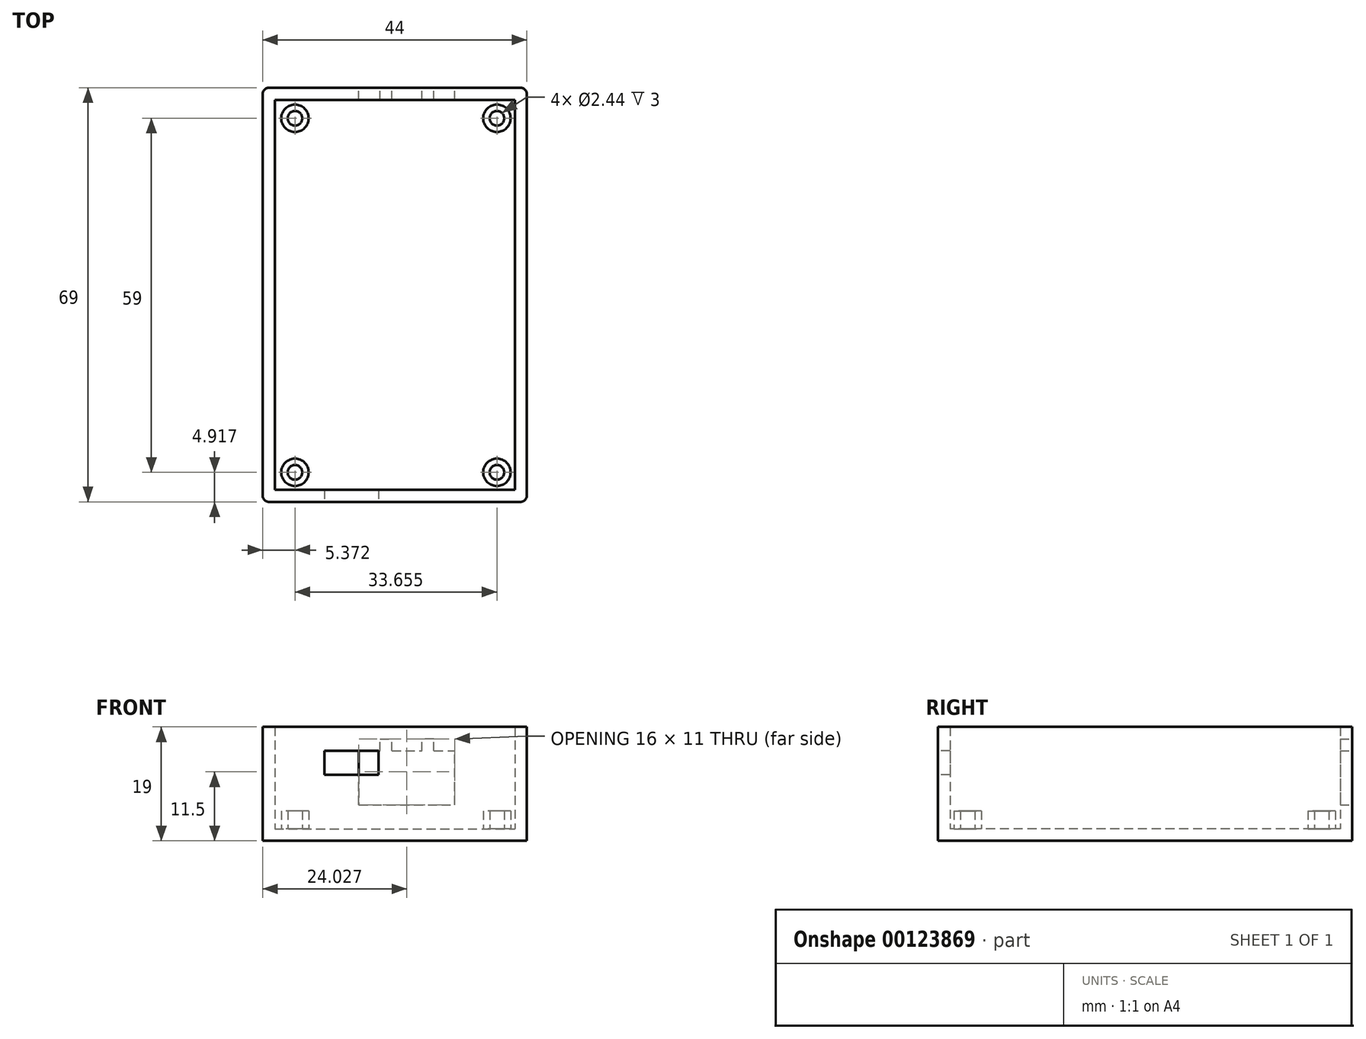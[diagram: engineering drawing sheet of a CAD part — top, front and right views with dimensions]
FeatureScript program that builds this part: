
annotation { "Feature Type Name" : "Feature", "Feature Type Description" : "" }
export const myFeature = defineFeature(function(context is Context, id is Id, definition is map)
    precondition{}
    {
        {
            var Q0;
            Q0=qCreatedBy(makeId("Top.planeOp"),FACE);
            var sketch = newSketch(context, id + "F0", { "sketchPlane" : qUnion([Q0])});
            skLineSegment(sketch, "E0.bottom", {"start": v(20, -32.5) * mm, "end": v(-20, -32.5) * mm});
            skLineSegment(sketch, "E0.top", {"start": v(20, 32.5) * mm, "end": v(-20, 32.5) * mm});
            skLineSegment(sketch, "E0.left", {"start": v(20, -32.5) * mm, "end": v(20, 32.5) * mm});
            skLineSegment(sketch, "E0.right", {"start": v(-20, -32.5) * mm, "end": v(-20, 32.5) * mm});
            skPoint(sketch, "E0.middle", {"position": v(0, 0) * mm});
            skLineSegment(sketch, "E1.0", {"start": v(21, 34.5) * mm, "end": v(-21, 34.5) * mm});
            skLineSegment(sketch, "E1.1", {"start": v(22, -33.5) * mm, "end": v(22, 33.5) * mm});
            skLineSegment(sketch, "E1.2", {"start": v(21, -34.5) * mm, "end": v(-21, -34.5) * mm});
            skLineSegment(sketch, "E1.3", {"start": v(-22, -33.5) * mm, "end": v(-22, 33.5) * mm});
            skCircle(sketch, "E2", {"center": v(-16.63, 29.42) * mm, "radius": 2.28 * mm});
            skCircle(sketch, "E3", {"center": v(-16.63, 29.42) * mm, "radius": 1.22 * mm});
            skCircle(sketch, "E4.0.1.0", {"center": v(-16.63, -29.58) * mm, "radius": 2.28 * mm});
            skCircle(sketch, "E4.0.1.1", {"center": v(-16.63, -29.58) * mm, "radius": 1.22 * mm});
            skCircle(sketch, "E4.1.0.0", {"center": v(17.03, 29.42) * mm, "radius": 2.28 * mm});
            skCircle(sketch, "E4.1.0.1", {"center": v(17.03, 29.42) * mm, "radius": 1.22 * mm});
            skCircle(sketch, "E4.1.1.0", {"center": v(17.03, -29.58) * mm, "radius": 2.28 * mm});
            skCircle(sketch, "E4.1.1.1", {"center": v(17.03, -29.58) * mm, "radius": 1.22 * mm});
            skLineSegment(sketch, "E4.direction1", {"start": v(-16.63, 29.42) * mm, "end": v(17.03, 29.42) * mm, "construction": true});
            skLineSegment(sketch, "E4.direction2", {"start": v(-16.63, 29.42) * mm, "end": v(-16.63, -29.58) * mm, "construction": true});
            skPoint(sketch, "E5.visualSharp", {"position": v(-22, 34.5) * mm});
            skArc(sketch, "E5.filletArc", {"start": v(-21, 34.5) * mm, "mid": v(-21.7, 34.2) * mm, "end": v(-22, 33.5) * mm});
            skPoint(sketch, "E6.visualSharp", {"position": v(22, 34.5) * mm});
            skArc(sketch, "E6.filletArc", {"start": v(22, 33.5) * mm, "mid": v(21.7, 34.2) * mm, "end": v(21, 34.5) * mm});
            skPoint(sketch, "E7.visualSharp", {"position": v(-22, -34.5) * mm});
            skArc(sketch, "E7.filletArc", {"start": v(-22, -33.5) * mm, "mid": v(-21.7, -34.2) * mm, "end": v(-21, -34.5) * mm});
            skPoint(sketch, "E8.visualSharp", {"position": v(22, -34.5) * mm});
            skArc(sketch, "E8.filletArc", {"start": v(21, -34.5) * mm, "mid": v(21.7, -34.2) * mm, "end": v(22, -33.5) * mm});
            skSolve(sketch);
        }
        {
            var Q0;
            Q0=makeQuery(id+"F0.imprint","IMPRINT",FACE,{"disambiguationData":[TD([[makeQuery(id+"F0.imprint","IMPRINT",EDGE,{"derivedFrom":sQuery(id+"F0.wireOp",EDGE,"E0.bottom")}),1.0]])]});
            var Q1;
            Q1=makeQuery(id+"F0.imprint","IMPRINT",FACE,{"disambiguationData":[TD([[makeQuery(id+"F0.imprint","IMPRINT",EDGE,{"derivedFrom":sQuery(id+"F0.wireOp",EDGE,"E0.bottom")}),-1.0]])]});
            var Q2;
            Q2=makeQuery(id+"F0.imprint","IMPRINT",FACE,{"disambiguationData":[TD([[makeQuery(id+"F0.imprint","IMPRINT",EDGE,{"derivedFrom":sQuery(id+"F0.wireOp",EDGE,"E4.0.1.1")}),1.0]])]});
            var Q3;
            Q3=makeQuery(id+"F0.imprint","IMPRINT",FACE,{"disambiguationData":[TD([[makeQuery(id+"F0.imprint","IMPRINT",EDGE,{"derivedFrom":sQuery(id+"F0.wireOp",EDGE,"E4.1.1.1")}),1.0]])]});
            var Q4;
            Q4=makeQuery(id+"F0.imprint","IMPRINT",FACE,{"disambiguationData":[TD([[makeQuery(id+"F0.imprint","IMPRINT",EDGE,{"derivedFrom":sQuery(id+"F0.wireOp",EDGE,"E4.1.1.0")}),1.0]])]});
            var Q5;
            Q5=makeQuery(id+"F0.imprint","IMPRINT",FACE,{"disambiguationData":[TD([[makeQuery(id+"F0.imprint","IMPRINT",EDGE,{"derivedFrom":sQuery(id+"F0.wireOp",EDGE,"E4.0.1.0")}),1.0]])]});
            var Q6;
            Q6=makeQuery(id+"F0.imprint","IMPRINT",FACE,{"disambiguationData":[TD([[makeQuery(id+"F0.imprint","IMPRINT",EDGE,{"derivedFrom":sQuery(id+"F0.wireOp",EDGE,"E4.1.0.0")}),1.0]])]});
            var Q7;
            Q7=makeQuery(id+"F0.imprint","IMPRINT",FACE,{"disambiguationData":[TD([[makeQuery(id+"F0.imprint","IMPRINT",EDGE,{"derivedFrom":sQuery(id+"F0.wireOp",EDGE,"E4.1.0.1")}),1.0]])]});
            var Q8;
            Q8=makeQuery(id+"F0.imprint","IMPRINT",FACE,{"disambiguationData":[TD([[makeQuery(id+"F0.imprint","IMPRINT",EDGE,{"derivedFrom":sQuery(id+"F0.wireOp",EDGE,"E2")}),1.0]])]});
            var Q9;
            Q9=makeQuery(id+"F0.imprint","IMPRINT",FACE,{"disambiguationData":[TD([[makeQuery(id+"F0.imprint","IMPRINT",EDGE,{"derivedFrom":sQuery(id+"F0.wireOp",EDGE,"E3")}),1.0]])]});
            extrude(context, id + "F1", {"entities" : qUnion([Q0, Q1, Q2, Q3, Q4, Q5, Q6, Q7, Q8, Q9]), "depth" : 2 * mm});
        }
        {
            var Q0;
            Q0=makeQuery(id+"F0.imprint","IMPRINT",FACE,{"disambiguationData":[TD([[makeQuery(id+"F0.imprint","IMPRINT",EDGE,{"derivedFrom":sQuery(id+"F0.wireOp",EDGE,"E0.bottom")}),1.0]])]});
            extrude(context, id + "F2", {"entities" : qUnion([Q0]), "operationType" : NewBodyOperationType.ADD, "depth" : 19 * mm});
        }
        {
            var Q0;
            Q0=makeQuery(id+"F0.imprint","IMPRINT",FACE,{"disambiguationData":[TD([[makeQuery(id+"F0.imprint","IMPRINT",EDGE,{"derivedFrom":sQuery(id+"F0.wireOp",EDGE,"E2")}),1.0]])]});
            var Q1;
            Q1=makeQuery(id+"F0.imprint","IMPRINT",FACE,{"disambiguationData":[TD([[makeQuery(id+"F0.imprint","IMPRINT",EDGE,{"derivedFrom":sQuery(id+"F0.wireOp",EDGE,"E4.1.0.0")}),1.0]])]});
            var Q2;
            Q2=makeQuery(id+"F0.imprint","IMPRINT",FACE,{"disambiguationData":[TD([[makeQuery(id+"F0.imprint","IMPRINT",EDGE,{"derivedFrom":sQuery(id+"F0.wireOp",EDGE,"E4.0.1.0")}),1.0]])]});
            var Q3;
            Q3=makeQuery(id+"F0.imprint","IMPRINT",FACE,{"disambiguationData":[TD([[makeQuery(id+"F0.imprint","IMPRINT",EDGE,{"derivedFrom":sQuery(id+"F0.wireOp",EDGE,"E4.1.1.0")}),1.0]])]});
            extrude(context, id + "F3", {"entities" : qUnion([Q0, Q1, Q2, Q3]), "operationType" : NewBodyOperationType.ADD, "depth" : 5 * mm});
        }
        {
            var Q0;
            {var subQ0=sQuery(id+"F0.wireOp",EDGE,"E1.0");Q0=makeQuery(id+"F2.boolean.opBoolean","MERGE",FACE,{"derivedFrom":[makeQuery(id+"F1.opExtrude","SWEPT_FACE",FACE,{"disambiguationData":[OSD([subQ0])]}),makeQuery(id+"F2.opExtrude","SWEPT_FACE",FACE,{"disambiguationData":[OSD([subQ0])]})]});}
            var sketch = newSketch(context, id + "F4", { "sketchPlane" : qUnion([Q0])});
            skLineSegment(sketch, "E9.bottom", {"start": v(5.97, 6) * mm, "end": v(-10.03, 6) * mm});
            skLineSegment(sketch, "E9.top", {"start": v(5.97, 15) * mm, "end": v(2.47, 15) * mm});
            skLineSegment(sketch, "E9.left", {"start": v(5.97, 6) * mm, "end": v(5.97, 15) * mm});
            skLineSegment(sketch, "E9.right", {"start": v(-10.03, 6) * mm, "end": v(-10.03, 15) * mm});
            skLineSegment(sketch, "E10.top", {"start": v(-6.53, 17) * mm, "end": v(-4.53, 17) * mm});
            skLineSegment(sketch, "E10.left", {"start": v(-6.53, 15) * mm, "end": v(-6.53, 17) * mm});
            skLineSegment(sketch, "E10.right", {"start": v(-4.53, 15) * mm, "end": v(-4.53, 17) * mm});
            skLineSegment(sketch, "E11.top", {"start": v(2.47, 17) * mm, "end": v(0.47, 17) * mm});
            skLineSegment(sketch, "E11.left", {"start": v(2.47, 15) * mm, "end": v(2.47, 17) * mm});
            skLineSegment(sketch, "E11.right", {"start": v(0.47, 15) * mm, "end": v(0.47, 17) * mm});
            skLineSegment(sketch, "E12.trimOffspring", {"start": v(0.47, 15) * mm, "end": v(-4.53, 15) * mm});
            skLineSegment(sketch, "E13.trimOffspring", {"start": v(-6.53, 15) * mm, "end": v(-10.03, 15) * mm});
            skSolve(sketch);
        }
        {
            var Q0;
            Q0=makeQuery(id+"F4.imprint","IMPRINT",FACE,{"disambiguationData":[TD([[makeQuery(id+"F4.imprint","IMPRINT",EDGE,{"derivedFrom":sQuery(id+"F4.wireOp",EDGE,"E9.bottom")}),-1.0]])]});
            extrude(context, id + "F5", {"entities" : qUnion([Q0]), "operationType" : NewBodyOperationType.REMOVE, "oppositeDirection" : true, "depth" : 5 * mm});
        }
        {
            var Q0;
            {var subQ0=sQuery(id+"F0.wireOp",EDGE,"E1.2");Q0=makeQuery(id+"F2.boolean.opBoolean","MERGE",FACE,{"derivedFrom":[makeQuery(id+"F1.opExtrude","SWEPT_FACE",FACE,{"disambiguationData":[OSD([subQ0])]}),makeQuery(id+"F2.opExtrude","SWEPT_FACE",FACE,{"disambiguationData":[OSD([subQ0])]})]});}
            var sketch = newSketch(context, id + "F6", { "sketchPlane" : qUnion([Q0])});
            skLineSegment(sketch, "E14.bottom", {"start": v(-11.73, 15) * mm, "end": v(-2.73, 15) * mm});
            skLineSegment(sketch, "E14.top", {"start": v(-11.73, 11) * mm, "end": v(-2.73, 11) * mm});
            skLineSegment(sketch, "E14.left", {"start": v(-11.73, 15) * mm, "end": v(-11.73, 11) * mm});
            skLineSegment(sketch, "E14.right", {"start": v(-2.73, 15) * mm, "end": v(-2.73, 11) * mm});
            skSolve(sketch);
        }
        {
            var Q0;
            Q0=makeQuery(id+"F6.imprint","IMPRINT",FACE,{"disambiguationData":[TD([[makeQuery(id+"F6.imprint","IMPRINT",EDGE,{"derivedFrom":sQuery(id+"F6.wireOp",EDGE,"E14.bottom")}),-1.0]])]});
            extrude(context, id + "F7", {"entities" : qUnion([Q0]), "operationType" : NewBodyOperationType.REMOVE, "oppositeDirection" : true, "depth" : 5 * mm});
        }
    });
